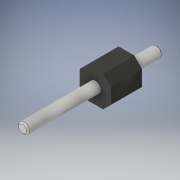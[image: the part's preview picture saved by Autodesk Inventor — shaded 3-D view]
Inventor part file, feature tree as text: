
AUTODESK INVENTOR PART (.ipt)
format: ipt  version: 2017 (Build 210142000, 142)  size: 120,320 bytes
history: native  units: in
note: dims shown in document units (in); Inventor stores cm internally (conversion verified against a paired STEP export)
features: extrude x2, chamfer x2, sketch x2
ambient origin geometry x8: Origin, YZ Plane, XZ Plane, XY Plane, X Axis, Y Axis, Z Axis, Center Point
bodies: Solid1 (feature_tree)
feature tree (6):
  extrude  "Extrusion1"  Depth=0.335in TaperAngle=0.0deg
  chamfer  "Chamfer1"  Distance=0.005in Angle=45.0deg
  extrude  "Extrusion2"  Depth=0.1in
  chamfer  "Chamfer2"  Distance=0.1in
  sketch  "Sketch1"  dims[d0=0.035in d1=0.335in d2=0.1in d3=0.0in d4=0.0in d5=0.005in d6=0.125in d7=45.0deg]
  sketch  "Sketch2"  dims[d8=0.1in d9=0.1in d10=0.1in d11=0.0in d12=0.025in d13=0.125in d14=45.0deg]
